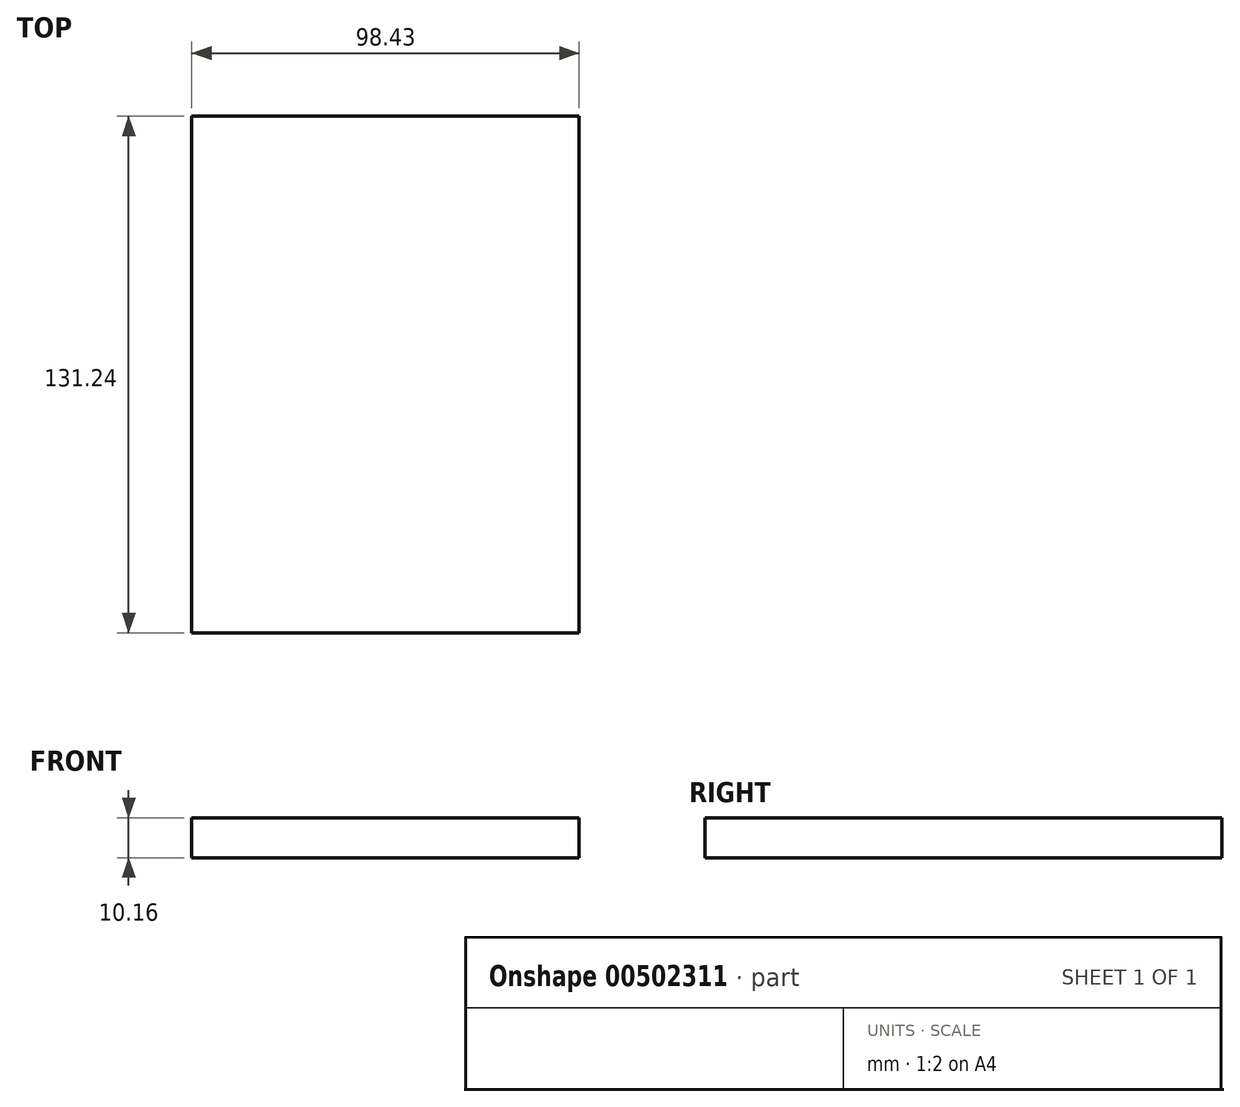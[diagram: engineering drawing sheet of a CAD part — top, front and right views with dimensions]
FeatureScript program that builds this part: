
annotation { "Feature Type Name" : "Feature", "Feature Type Description" : "" }
export const myFeature = defineFeature(function(context is Context, id is Id, definition is map)
    precondition{}
    {
        {
            var Q0;
            Q0=qCreatedBy(makeId("Top.planeOp"),FACE);
            var sketch = newSketch(context, id + "F0", { "sketchPlane" : qUnion([Q0])});
            skLineSegment(sketch, "E0", {"start": v(0, 0) * mm, "end": v(0, 131.24) * mm});
            skLineSegment(sketch, "E1", {"start": v(0, 131.24) * mm, "end": v(98.43, 131.24) * mm});
            skLineSegment(sketch, "E2", {"start": v(98.43, 131.24) * mm, "end": v(98.43, 0) * mm});
            skLineSegment(sketch, "E3", {"start": v(98.43, 0) * mm, "end": v(0, 0) * mm});
            skSolve(sketch);
        }
        {
            var Q0;
            Q0=makeQuery(id+"F0.imprint","IMPRINT",FACE,{"disambiguationData":[TD([[makeQuery(id+"F0.imprint","IMPRINT",EDGE,{"derivedFrom":sQuery(id+"F0.wireOp",EDGE,"E0")}),-1.0]])]});
            extrude(context, id + "F1", {"entities" : qUnion([Q0]), "depth" : 10.16 * mm});
        }
    });
